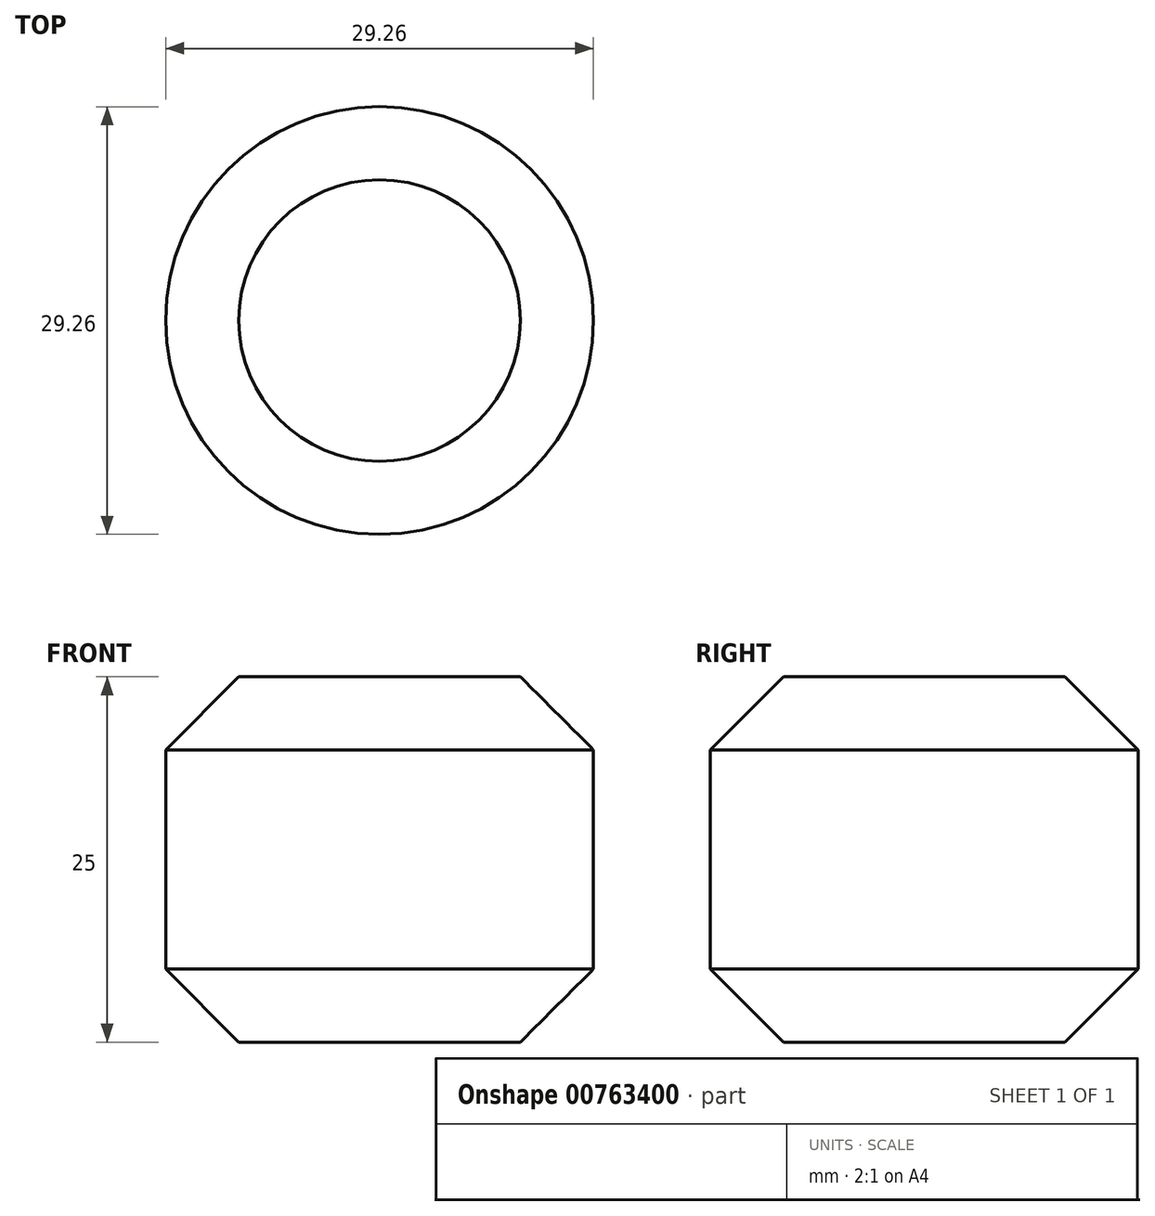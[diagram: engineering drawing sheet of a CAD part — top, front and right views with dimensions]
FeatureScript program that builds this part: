
annotation { "Feature Type Name" : "Feature", "Feature Type Description" : "" }
export const myFeature = defineFeature(function(context is Context, id is Id, definition is map)
    precondition{}
    {
        {
            var Q0;
            Q0=qCreatedBy(makeId("Top.planeOp"),FACE);
            var sketch = newSketch(context, id + "F0", { "sketchPlane" : qUnion([Q0])});
            skCircle(sketch, "E0", {"center": v(0, 0) * mm, "radius": 14.63 * mm});
            skSolve(sketch);
        }
        {
            var Q0;
            Q0=makeQuery(id+"F0.imprint","IMPRINT",FACE,{"disambiguationData":[TD([[makeQuery(id+"F0.imprint","IMPRINT",EDGE,{"derivedFrom":sQuery(id+"F0.wireOp",EDGE,"E0")}),1.0]])]});
            extrude(context, id + "F1", {"entities" : qUnion([Q0]), "endBound" : BoundingType.SYMMETRIC, "depth" : 25 * mm, "offsetDistance" : 25 * mm});
        }
        {
            var Q0;
            Q0=makeQuery(id+"F1.opExtrude","SWEPT_FACE",FACE,{"disambiguationData":[OSD([sQuery(id+"F0.wireOp",EDGE,"E0")])]});
            chamfer(context, id + "F2", {"entities" : qUnion([Q0]), "width" : 5 * mm, "tangentPropagation" : true});
        }
    });
